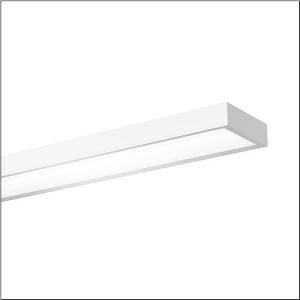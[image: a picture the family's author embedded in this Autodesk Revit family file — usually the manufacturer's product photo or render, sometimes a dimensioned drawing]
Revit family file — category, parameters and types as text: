
# Revit family: sport_31_51hs12dc4eca
name_source: partatom
category: Lighting Fixtures
units: mm (PartAtom-declared; Revit-internal decimal feet)

## family parameters
Cut with Voids When Loaded = No
Host = Face
Light Source = No
Part Type = Normal
Room Calculation Point = No
Round Connector Dimension = Use Diameter
Shared = No

## types (1)
- --- (1 x LED, 11990 lm, 89.4 W, 4000K)
    Apparent Load = 89 VA
    CIE Flux Codes = 65 89 97 100 100
    Color Rendering = 80
    Color Temperature = 4000K
    Default Elevation = 1800 mm
    Description = Sport 31, LED high bay luminaire, primary light control with reflector, of sheet steel, primary anti-glare with prismatic structure, of PC, primary optical cover: cover panel, of PC, light emission: direct distribution, primary light characteristic: symmetric, installation type: suspended mounting, recessed, surface-mounted, LED, rated luminous flux: 12.000lm, luminous efficacy: 137lm/W, light colour: 840, colour temperature: 4000K, control gear: ECG DALI, with terminal, 5-pole, max. 2.5mm², mains connection: 220..240V, AC/DC, 50/60Hz, rated input power: 88W, housing, of sheet steel, traffic white (RAL 9016), length: 1.540mm, width: 315mm, height: 95mm, protection rating (complete): IP20, protection rating (lamp compartment, on room side): IP50, insulation class (complete): insulation class I (protective earthing), certification: CE, ENEC, UKCA, ball protection: ball impact resistant with ceiling mounting or chain suspension, impact resistance: IK08, permissible operating ambient temperature: -20..+35°C, standard: DIN 18032-3, EN 60598-2-22, packaging unit: 1 piece
    Height = 100 mm  [stored 0.328084 ft]
    Lamp = 1 x LED
    Lamp Light Flux = 11990 lm
    Lamp Power = 89.4 W
    Lamp count = 1
    Length = 1500 mm
    Luminous efficacy = 134 lm/W
    Manufacturer = Siteco
    ModVariant = No
    Model = 51HS12DC4ECA
    Mounting Place = Ceiling
    Mounting Type = Pendant
    Number of Poles = 1
    OnlyDefault = Yes
    Power Factor = 1
    Product Name = Sport 31
    Product group = LED high bay luminaire
    ProductGroupID = 903
    Protection Class = Protection class I
    Protection Degree = IP 20
    RLX_Detail_Level = 1
    RLX_Emergency_Light_Flux = 0 lm
    RLX_Emergency_Type = 0
    RLX_Emergency_Type_DB = No
    RlxData = <blob elided: 22849 chars, md5=a54b6b2e>
    Socket = socket
    Standby Power = 0 W
    System Light Flux = 11990 lm
    System Power = 89 W
    Type Comments = factory setting: luminous flux: 100 % | dim-lin: 254 | 380 mA
    Type Image = l_1006823.jpg
    URL = http://relux.com
    VarID = @adj_150961
    Voltage = 0 V
    Weight = 0.00 kg
    Width = 315 mm

note: [stored X ft] marks values corroborated as IEEE doubles in the binary element streams (Revit-internal decimal feet)

## geometry (parser evidence)
native form markers: Blend x4, Sweep x10
no freeform markers — native parametric forms only
